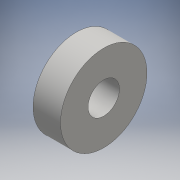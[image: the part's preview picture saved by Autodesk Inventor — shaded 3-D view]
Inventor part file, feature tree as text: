
AUTODESK INVENTOR PART (.ipt)
format: ipt  version: 2016 (Build 200138000, 138)  size: 99,840 bytes
history: native  units: mm
features: extrude x1, plane x1, sketch x1
ambient origin geometry x8: Origin, YZ Plane, XZ Plane, XY Plane, X Axis, Y Axis, Z Axis, Center Point
bodies: Solid1 (feature_tree)
feature tree (3):
  extrude  "Extrusion1"  Depth=7.0mm
  plane  "Work Plane1"
  sketch  "Sketch1"  dims[d0=8.0mm d1=22.0mm d2=7.0mm d3=0.0mm d4=-3.5mm]
